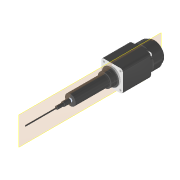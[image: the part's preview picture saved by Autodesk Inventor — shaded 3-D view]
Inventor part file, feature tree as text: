
AUTODESK INVENTOR PART (.ipt)
format: ipt  version: 2022 (Build 260153000, 153)  size: 344,576 bytes
history: native  units: in
note: dims shown in document units (in); Inventor stores cm internally (conversion verified against a paired STEP export)
features: extrude x3, sketch x3, other x2, plane x1
ambient origin geometry x8: Origin, YZ Plane, XZ Plane, XY Plane, X Axis, Y Axis, Z Axis, Center Point
bodies: Solid2 (feature_tree), Solid3 (feature_tree), Solid4 (feature_tree), Solid1 (feature_tree)
feature tree (9):
  extrude  "Extrusion2"  Depth=0.2756in TaperAngle=0.0deg
  extrude  "Extrusion3"  Depth=1.2598in TaperAngle=0.0deg
  extrude  "Extrusion4"  Depth=1.6535in TaperAngle=0.0deg
  plane  "Arbeitsebene1"
  sketch  "Skizze2"  dims[d3=0.5043in d4=0.2756in d5=0.0in]
  sketch  "Skizze3"  dims[d6=0.3937in d7=1.2598in d8=0.0in]
  sketch  "Skizze4"  dims[d9=0.0394in d10=1.6535in d11=0.0in]
  other  "Solid2:1"
  other  "Solid3:1"
